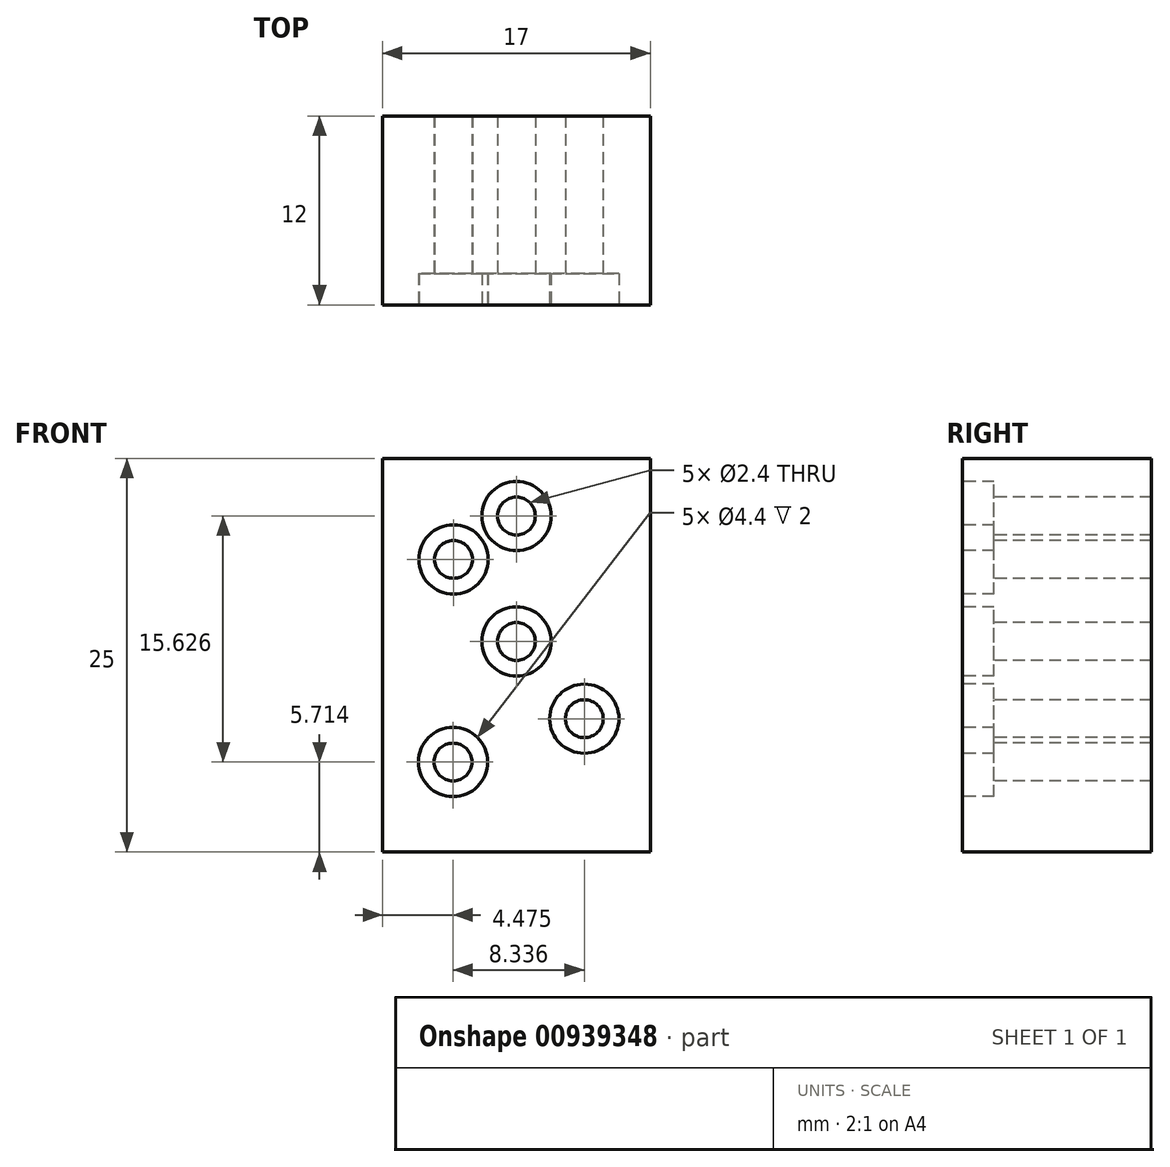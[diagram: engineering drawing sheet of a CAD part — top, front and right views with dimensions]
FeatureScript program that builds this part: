
annotation { "Feature Type Name" : "Feature", "Feature Type Description" : "" }
export const myFeature = defineFeature(function(context is Context, id is Id, definition is map)
    precondition{}
    {
        {
            var Q0;
            Q0=qCreatedBy(makeId("Top.planeOp"),FACE);
            var sketch = newSketch(context, id + "F0", { "sketchPlane" : qUnion([Q0])});
            skLineSegment(sketch, "E0.bottom", {"start": v(-10, 5) * mm, "end": v(10, 5) * mm});
            skLineSegment(sketch, "E0.top", {"start": v(-10, -5) * mm, "end": v(10, -5) * mm});
            skLineSegment(sketch, "E0.left", {"start": v(-10, 5) * mm, "end": v(-10, -5) * mm});
            skLineSegment(sketch, "E0.right", {"start": v(10, 5) * mm, "end": v(10, -5) * mm});
            skPoint(sketch, "E0.middle", {"position": v(0, 0) * mm});
            skLineSegment(sketch, "E1", {"start": v(15.96, 26.47) * mm, "end": v(28.28, 18.97) * mm, "construction": true});
            skLineSegment(sketch, "E2", {"start": v(28.28, 18.97) * mm, "end": v(33.28, 0) * mm, "construction": true});
            skLineSegment(sketch, "E3", {"start": v(-10.5, 20) * mm, "end": v(-1.68, 20) * mm});
            skArc(sketch, "E4", {"start": v(3.02, 13.29) * mm, "mid": v(2.41, 17.87) * mm, "end": v(-1.68, 20) * mm});
            skLineSegment(sketch, "E5", {"start": v(3.02, 13.29) * mm, "end": v(0, 5) * mm});
            skLineSegment(sketch, "E6", {"start": v(-10.5, 20) * mm, "end": v(0, 5) * mm});
            skSolve(sketch);
        }
        {
            var Q0;
            Q0=makeQuery(id+"F0.imprint","IMPRINT",FACE,{"disambiguationData":[TD([[makeQuery(id+"F0.imprint","IMPRINT",EDGE,{"derivedFrom":sQuery(id+"F0.wireOp",EDGE,"E0.top")}),1.0]])]});
            var Q1;
            Q1=sQuery(id+"F0.wireOp",EDGE,"E4");
            var Q2;
            Q2=sQuery(id+"F0.wireOp",EDGE,"E3");
            extrude(context, id + "F1", {"entities" : qUnion([Q0]), "bodyType" : ToolBodyType.SURFACE, "surfaceEntities" : qUnion([Q1, Q2]), "depth" : 25 * mm, "offsetDistance" : 25 * mm});
        }
        {
            var Q0;
            Q0=qCreatedBy(makeId("Top.planeOp"),FACE);
            var sketch = newSketch(context, id + "F2", { "sketchPlane" : qUnion([Q0])});
            skLineSegment(sketch, "E7.bottom", {"start": v(-8.5, 10) * mm, "end": v(8.5, 10) * mm});
            skLineSegment(sketch, "E7.top", {"start": v(-8.5, 22) * mm, "end": v(8.5, 22) * mm});
            skLineSegment(sketch, "E7.left", {"start": v(-8.5, 10) * mm, "end": v(-8.5, 22) * mm});
            skLineSegment(sketch, "E7.right", {"start": v(8.5, 10) * mm, "end": v(8.5, 22) * mm});
            skLineSegment(sketch, "E8", {"start": v(0, 10) * mm, "end": v(0, 0) * mm, "construction": true});
            skSolve(sketch);
        }
        {
            var Q0;
            Q0=makeQuery(id+"F2.imprint","IMPRINT",FACE,{"disambiguationData":[TD([[makeQuery(id+"F2.imprint","IMPRINT",EDGE,{"derivedFrom":sQuery(id+"F2.wireOp",EDGE,"E7.bottom")}),1.0]])]});
            extrude(context, id + "F3", {"entities" : qUnion([Q0]), "depth" : 25 * mm, "offsetDistance" : 25 * mm});
        }
        {
            var Q0;
            Q0=makeQuery(id+"F3.opExtrude","SWEPT_FACE",FACE,{"disambiguationData":[OSD([sQuery(id+"F2.wireOp",EDGE,"E7.bottom")])]});
            var sketch = newSketch(context, id + "F4", { "sketchPlane" : qUnion([Q0])});
            skPoint(sketch, "E9", {"position": v(-4, 18.58) * mm});
            skPoint(sketch, "E10", {"position": v(0, 21.34) * mm});
            skPoint(sketch, "E11", {"position": v(0, 13.37) * mm});
            skPoint(sketch, "E12", {"position": v(4.31, 8.46) * mm});
            skPoint(sketch, "E13", {"position": v(-4.02, 5.71) * mm});
            skLineSegment(sketch, "E14", {"start": v(0, 25) * mm, "end": v(0, 0) * mm, "construction": true});
            skSolve(sketch);
        }
        {
            var Q0;
            Q0=sQuery(id+"F4.wireOp",VERTEX,"E9");
            var Q1;
            Q1=sQuery(id+"F4.wireOp",VERTEX,"E10");
            var Q2;
            Q2=sQuery(id+"F4.wireOp",VERTEX,"E11");
            var Q3;
            Q3=sQuery(id+"F4.wireOp",VERTEX,"E12");
            var Q4;
            Q4=sQuery(id+"F4.wireOp",VERTEX,"E13");
            var Q5;
            Q5=makeQuery(id+"F3.opExtrude","SWEPT_BODY",BODY,{"disambiguationData":[OSD([sQuery(id+"F2.wireOp",EDGE,"E7.bottom"),sQuery(id+"F2.wireOp",EDGE,"E7.top"),sQuery(id+"F2.wireOp",EDGE,"E7.left"),sQuery(id+"F2.wireOp",EDGE,"E7.right")])]});
            hole(context, id + "F5", {"style" : HoleStyle.C_BORE, "endStyle" : HoleEndStyle.BLIND, "standardTappedOrClearance" : lookupTablePath({ "fit" : "Normal", "standard" : "ISO", "size" : "M2", "type" : "Clearance" }), "standardBlindInLast" : lookupTablePath({ "fit" : "Normal", "standard" : "ISO", "engagement" : "75%", "pitch" : "0.25 mm", "size" : "M2", "type" : "Clearance & tapped" }), "holeDiameter" : 2.4 * mm, "cBoreDiameter" : 4.4 * mm, "cBoreDepth" : 2 * mm, "majorDiameter" : 5 * mm, "holeDepth" : 12 * mm, "isTappedThrough" : true, "tappedDepth" : 12 * mm, "tapClearance" : 3, "locations" : qUnion([Q0, Q1, Q2, Q3, Q4]), "scope" : qUnion([Q5])});
        }
    });
